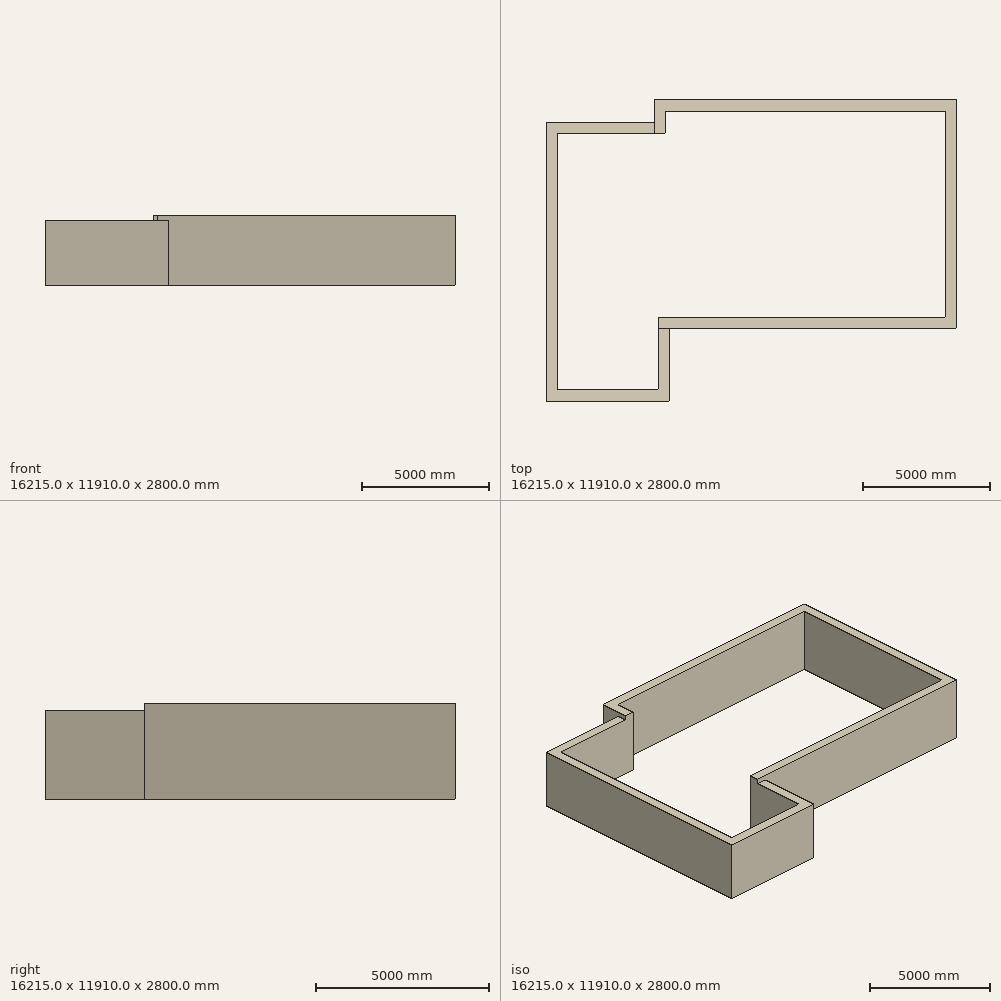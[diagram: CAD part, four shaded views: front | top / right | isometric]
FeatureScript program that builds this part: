
annotation { "Feature Type Name" : "Feature", "Feature Type Description" : "" }
export const myFeature = defineFeature(function(context is Context, id is Id, definition is map)
    precondition{}
    {
        {
            var Q0;
            Q0=qCreatedBy(makeId("Top.planeOp"),FACE);
            var sketch = newSketch(context, id + "F0", { "sketchPlane" : qUnion([Q0])});
            skLineSegment(sketch, "E0", {"start": v(0, 0) * mm, "end": v(11360, 0) * mm});
            skLineSegment(sketch, "E1", {"start": v(11360, 0) * mm, "end": v(11360, 9030) * mm});
            skLineSegment(sketch, "E2", {"start": v(11360, 9030) * mm, "end": v(-580, 9030) * mm});
            skLineSegment(sketch, "E3", {"start": v(0, 0) * mm, "end": v(0, -2880) * mm});
            skLineSegment(sketch, "E4", {"start": v(-140, 8590) * mm, "end": v(-140, 7700) * mm});
            skLineSegment(sketch, "E5", {"start": v(-140, 7700) * mm, "end": v(-200, 7700) * mm});
            skLineSegment(sketch, "E6", {"start": v(-200, 7700) * mm, "end": v(-200, 440) * mm});
            skLineSegment(sketch, "E7", {"start": v(-440, 0) * mm, "end": v(-440, 7700) * mm});
            skLineSegment(sketch, "E8", {"start": v(-440, 7700) * mm, "end": v(-580, 7700) * mm});
            skLineSegment(sketch, "E9", {"start": v(10920, 8590) * mm, "end": v(-140, 8590) * mm});
            skLineSegment(sketch, "E10", {"start": v(10920, 440) * mm, "end": v(10920, 8590) * mm});
            skLineSegment(sketch, "E11", {"start": v(10920, 440) * mm, "end": v(-200, 440) * mm});
            skLineSegment(sketch, "E12", {"start": v(-580, 9030) * mm, "end": v(-580, 8130) * mm});
            skLineSegment(sketch, "E13", {"start": v(-440, 0) * mm, "end": v(0, 0) * mm});
            skLineSegment(sketch, "E14", {"start": v(-580, 8130) * mm, "end": v(-580, 7700) * mm});
            skLineSegment(sketch, "E15", {"start": v(-580, 8130) * mm, "end": v(-4855, 8130) * mm});
            skLineSegment(sketch, "E16", {"start": v(-4855, 8130) * mm, "end": v(-4855, -2880) * mm});
            skLineSegment(sketch, "E17", {"start": v(-580, 7700) * mm, "end": v(-4415, 7700) * mm});
            skLineSegment(sketch, "E18", {"start": v(-4415, 7700) * mm, "end": v(-4415, -2440) * mm});
            skLineSegment(sketch, "E19", {"start": v(-4415, -2440) * mm, "end": v(-440, -2440) * mm});
            skLineSegment(sketch, "E20", {"start": v(-440, 7700) * mm, "end": v(-200, 7700) * mm});
            skLineSegment(sketch, "E21", {"start": v(-200, 440) * mm, "end": v(-440, 440) * mm});
            skLineSegment(sketch, "E22", {"start": v(0, 218.1) * mm, "end": v(-640, 218.1) * mm, "construction": true});
            skLineSegment(sketch, "E23", {"start": v(0, 218.1) * mm, "end": v(160, 218.1) * mm, "construction": true});
            skLineSegment(sketch, "E24", {"start": v(-440, -2440) * mm, "end": v(-440, 0) * mm});
            skLineSegment(sketch, "E25", {"start": v(-4855, -2880) * mm, "end": v(0, -2880) * mm});
            skSolve(sketch);
        }
        {
            var Q0;
            Q0=makeQuery(id+"F0.imprint","IMPRINT",FACE,{"disambiguationData":[TD([[makeQuery(id+"F0.imprint","IMPRINT",EDGE,{"derivedFrom":sQuery(id+"F0.wireOp",EDGE,"E0")}),1.0]])]});
            extrude(context, id + "F1", {"entities" : qUnion([Q0]), "depth" : 2800 * mm});
        }
        {
            var Q0;
            Q0=makeQuery(id+"F0.imprint","IMPRINT",FACE,{"disambiguationData":[TD([[makeQuery(id+"F0.imprint","IMPRINT",EDGE,{"derivedFrom":sQuery(id+"F0.wireOp",EDGE,"E3")}),-1.0]])]});
            extrude(context, id + "F2", {"entities" : qUnion([Q0]), "operationType" : NewBodyOperationType.ADD, "depth" : 2600 * mm});
        }
    });
